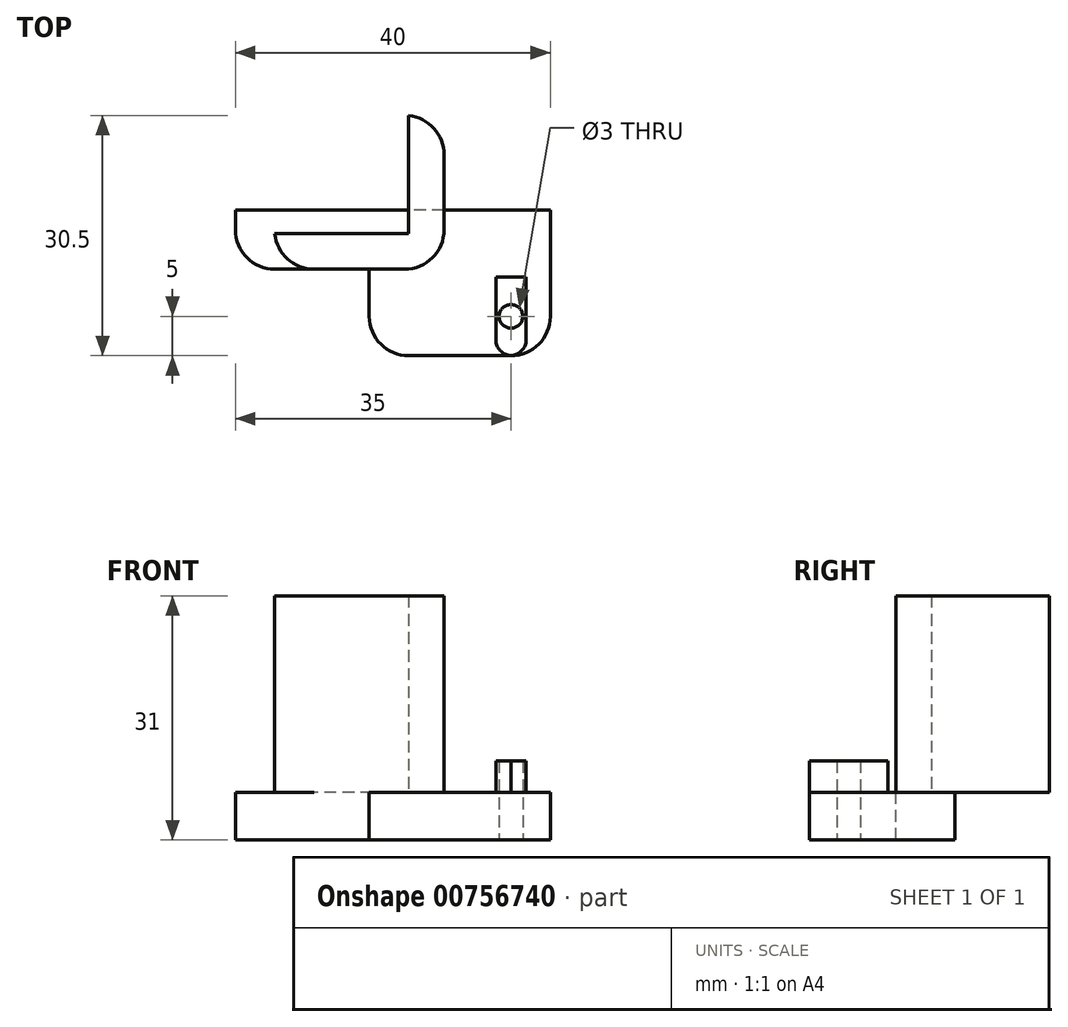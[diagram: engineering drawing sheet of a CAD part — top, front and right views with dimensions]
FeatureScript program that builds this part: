
annotation { "Feature Type Name" : "Feature", "Feature Type Description" : "" }
export const myFeature = defineFeature(function(context is Context, id is Id, definition is map)
    precondition{}
    {
        {
            var Q0;
            Q0=qCreatedBy(makeId("Front.planeOp"),FACE);
            var sketch = newSketch(context, id + "F0", { "sketchPlane" : qUnion([Q0])});
            skLineSegment(sketch, "E0.bottom", {"start": v(11.5, -3) * mm, "end": v(-11.5, -3) * mm});
            skLineSegment(sketch, "E0.top", {"start": v(11.5, 3) * mm, "end": v(-11.5, 3) * mm});
            skLineSegment(sketch, "E0.left", {"start": v(11.5, -3) * mm, "end": v(11.5, 3) * mm});
            skLineSegment(sketch, "E0.right", {"start": v(-11.5, -3) * mm, "end": v(-11.5, 3) * mm});
            skPoint(sketch, "E0.middle", {"position": v(0, 0) * mm});
            skSolve(sketch);
        }
        {
            var Q0;
            Q0=makeQuery(id+"F0.imprint","IMPRINT",FACE,{"disambiguationData":[TD([[makeQuery(id+"F0.imprint","IMPRINT",EDGE,{"derivedFrom":sQuery(id+"F0.wireOp",EDGE,"E0.bottom")}),-1.0]])]});
            extrude(context, id + "F1", {"entities" : qUnion([Q0]), "oppositeDirection" : true, "depth" : 11 * mm, "offsetDistance" : 25 * mm});
        }
        {
            var Q0;
            Q0=makeQuery(id+"F1.opExtrude","SWEPT_FACE",FACE,{"disambiguationData":[OSD([sQuery(id+"F0.wireOp",EDGE,"E0.top")])]});
            var sketch = newSketch(context, id + "F2", { "sketchPlane" : qUnion([Q0])});
            skLineSegment(sketch, "E1", {"start": v(6.5, 0) * mm, "end": v(6.5, 11) * mm, "construction": true});
            skLineSegment(sketch, "E2", {"start": v(-11.5, 5) * mm, "end": v(11.5, 5) * mm, "construction": true});
            skCircle(sketch, "E3", {"center": v(6.5, 5) * mm, "radius": 1.5 * mm});
            skLineSegment(sketch, "E4.bottom", {"start": v(8.42, 9.98) * mm, "end": v(4.58, 9.98) * mm});
            skLineSegment(sketch, "E4.top", {"start": v(8.42, 0.02) * mm, "end": v(4.58, 0.02) * mm});
            skLineSegment(sketch, "E4.left", {"start": v(8.42, 9.98) * mm, "end": v(8.42, 0.02) * mm});
            skLineSegment(sketch, "E4.right", {"start": v(4.58, 9.98) * mm, "end": v(4.58, 0.02) * mm});
            skSolve(sketch);
        }
        {
            var Q0;
            Q0=makeQuery(id+"F2.imprint","IMPRINT",FACE,{"disambiguationData":[TD([[makeQuery(id+"F2.imprint","IMPRINT",EDGE,{"derivedFrom":sQuery(id+"F2.wireOp",EDGE,"E3")}),-1.0]])]});
            extrude(context, id + "F3", {"entities" : qUnion([Q0]), "operationType" : NewBodyOperationType.ADD, "depth" : 4 * mm, "offsetDistance" : 25 * mm});
        }
        {
            var Q0;
            Q0=makeQuery(id+"F3.boolean.opBoolean","SPLIT",FACE,{"disambiguationData":[TD([makeQuery(id+"F3.opExtrude","SWEPT_FACE",FACE,{"disambiguationData":[OSD([sQuery(id+"F2.wireOp",EDGE,"E3")])]})])],"derivedFrom":makeQuery(id+"F1.opExtrude","SWEPT_FACE",FACE,{"disambiguationData":[OSD([sQuery(id+"F0.wireOp",EDGE,"E0.top")])]})});
            extrude(context, id + "F4", {"entities" : qUnion([Q0]), "operationType" : NewBodyOperationType.REMOVE, "oppositeDirection" : true, "depth" : 6 * mm, "offsetDistance" : 25 * mm});
        }
        {
            var Q0;
            Q0=makeQuery(id+"F3.opExtrude","SWEPT_EDGE",EDGE,{"disambiguationData":[OSD([sQuery(id+"F2.wireOp",EDGE,"E4.top"),sQuery(id+"F2.wireOp",EDGE,"E4.left")])]});
            var Q1;
            Q1=makeQuery(id+"F3.opExtrude","SWEPT_EDGE",EDGE,{"disambiguationData":[OSD([sQuery(id+"F2.wireOp",EDGE,"E4.top"),sQuery(id+"F2.wireOp",EDGE,"E4.right")])]});
            fillet(context, id + "F5", {"entities" : qUnion([Q0, Q1]), "radius" : 2 * mm, "tangentPropagation" : true, "allowEdgeOverflow" : false});
        }
        {
            var Q0;
            Q0=makeQuery(id+"F1.opExtrude","CAP_FACE",FACE,{"disambiguationData":[OSD([sQuery(id+"F0.wireOp",EDGE,"E0.bottom"),sQuery(id+"F0.wireOp",EDGE,"E0.top"),sQuery(id+"F0.wireOp",EDGE,"E0.left"),sQuery(id+"F0.wireOp",EDGE,"E0.right")])],"isStart":false});
            var sketch = newSketch(context, id + "F6", { "sketchPlane" : qUnion([Q0])});
            skLineSegment(sketch, "E5.bottom", {"start": v(-11.5, 3) * mm, "end": v(28.5, 3) * mm});
            skLineSegment(sketch, "E5.top", {"start": v(-11.5, -3) * mm, "end": v(28.5, -3) * mm});
            skLineSegment(sketch, "E5.left", {"start": v(-11.5, 3) * mm, "end": v(-11.5, -3) * mm});
            skLineSegment(sketch, "E5.right", {"start": v(28.5, 3) * mm, "end": v(28.5, -3) * mm});
            skSolve(sketch);
        }
        {
            var Q0;
            {var subQ0=sQuery(id+"F6.wireOp",EDGE,"E5.left");Q0=makeQuery(id+"F6.imprint","IMPRINT",FACE,{"disambiguationData":[TD([[makeQuery(id+"F6.imprint","IMPRINT",EDGE,{"derivedFrom":subQ0}),-1.0]])]});}
            var Q1;
            {var subQ2=sQuery(id+"F6.wireOp",EDGE,"E5.right");Q1=makeQuery(id+"F6.imprint","IMPRINT",FACE,{"disambiguationData":[TD([[makeQuery(id+"F6.imprint","IMPRINT",EDGE,{"derivedFrom":subQ2}),-1.0]])]});}
            extrude(context, id + "F7", {"entities" : qUnion([Q0, Q1]), "operationType" : NewBodyOperationType.ADD, "depth" : 4.5 * mm, "offsetDistance" : 25 * mm});
        }
        {
            var Q0;
            {var subQ1=sQuery(id+"F0.wireOp",EDGE,"E0.left");var subQ2=sQuery(id+"F0.wireOp",EDGE,"E0.top");Q0=makeQuery(id+"F7.boolean.opBoolean","MERGE",FACE,{"derivedFrom":[makeQuery(id+"F3.boolean.opBoolean","SPLIT",FACE,{"disambiguationData":[TD([makeQuery(id+"F1.opExtrude","SWEPT_FACE",FACE,{"disambiguationData":[OSD([subQ1])]})])],"derivedFrom":makeQuery(id+"F1.opExtrude","SWEPT_FACE",FACE,{"disambiguationData":[OSD([subQ2])]})}),makeQuery(id+"F7.opExtrude","SWEPT_FACE",FACE,{"disambiguationData":[OSD([sQuery(id+"F6.wireOp",EDGE,"E5.bottom")])]})]});}
            var sketch = newSketch(context, id + "F8", { "sketchPlane" : qUnion([Q0])});
            skLineSegment(sketch, "E6.bottom", {"start": v(-11.5, 11) * mm, "end": v(-23.5, 11) * mm});
            skLineSegment(sketch, "E6.top", {"start": v(-11.5, 15.5) * mm, "end": v(-23.5, 15.5) * mm});
            skLineSegment(sketch, "E6.left", {"start": v(-11.5, 11) * mm, "end": v(-11.5, 15.5) * mm});
            skLineSegment(sketch, "E6.right", {"start": v(-23.5, 11) * mm, "end": v(-23.5, 15.5) * mm});
            skLineSegment(sketch, "E7.bottom", {"start": v(-11.5, 11) * mm, "end": v(-6.5, 11) * mm});
            skLineSegment(sketch, "E7.top", {"start": v(-11.5, 15.5) * mm, "end": v(-6.5, 15.5) * mm});
            skLineSegment(sketch, "E7.right", {"start": v(-6.5, 11) * mm, "end": v(-6.5, 15.5) * mm});
            skSolve(sketch);
        }
        {
            var Q0;
            Q0=makeQuery(id+"F8.imprint","IMPRINT",FACE,{"disambiguationData":[TD([[makeQuery(id+"F8.imprint","IMPRINT",EDGE,{"derivedFrom":sQuery(id+"F8.wireOp",EDGE,"E6.bottom")}),-1.0]])]});
            var Q1;
            Q1=makeQuery(id+"F8.imprint","IMPRINT",FACE,{"disambiguationData":[TD([[makeQuery(id+"F8.imprint","IMPRINT",EDGE,{"derivedFrom":sQuery(id+"F8.wireOp",EDGE,"E7.bottom")}),1.0]])]});
            extrude(context, id + "F9", {"entities" : qUnion([Q0, Q1]), "operationType" : NewBodyOperationType.ADD, "depth" : 25 * mm, "offsetDistance" : 25 * mm});
        }
        {
            var Q0;
            Q0=makeQuery(id+"F9.boolean.opBoolean","MERGE",FACE,{"derivedFrom":[makeQuery(id+"F7.opExtrude","CAP_FACE",FACE,{"disambiguationData":[OSD([sQuery(id+"F6.wireOp",EDGE,"E5.bottom"),sQuery(id+"F6.wireOp",EDGE,"E5.top"),sQuery(id+"F6.wireOp",EDGE,"E5.left"),sQuery(id+"F6.wireOp",EDGE,"E5.right")])],"isStart":false}),makeQuery(id+"F9.opExtrude","SWEPT_FACE",FACE,{"disambiguationData":[OSD([sQuery(id+"F8.wireOp",EDGE,"E6.top"),sQuery(id+"F8.wireOp",EDGE,"E7.top")])]})]});
            var sketch = newSketch(context, id + "F10", { "sketchPlane" : qUnion([Q0])});
            skLineSegment(sketch, "E8.bottom", {"start": v(-11.5, 3) * mm, "end": v(28.5, 3) * mm});
            skLineSegment(sketch, "E8.top", {"start": v(-11.5, -3) * mm, "end": v(28.5, -3) * mm});
            skLineSegment(sketch, "E8.left", {"start": v(-11.5, 3) * mm, "end": v(-11.5, -3) * mm});
            skLineSegment(sketch, "E8.right", {"start": v(28.5, 3) * mm, "end": v(28.5, -3) * mm});
            skSolve(sketch);
        }
        {
            var Q0;
            Q0=makeQuery(id+"F10.imprint","IMPRINT",FACE,{"disambiguationData":[TD([[makeQuery(id+"F10.imprint","IMPRINT",EDGE,{"derivedFrom":sQuery(id+"F10.wireOp",EDGE,"E8.top")}),1.0]])]});
            extrude(context, id + "F11", {"entities" : qUnion([Q0]), "operationType" : NewBodyOperationType.ADD, "depth" : 3 * mm, "offsetDistance" : 25 * mm});
        }
        {
            var Q0;
            Q0=makeQuery(id+"F9.opExtrude","SWEPT_FACE",FACE,{"disambiguationData":[OSD([sQuery(id+"F8.wireOp",EDGE,"E7.right")])]});
            var sketch = newSketch(context, id + "F12", { "sketchPlane" : qUnion([Q0])});
            skLineSegment(sketch, "E9.bottom", {"start": v(11, 28) * mm, "end": v(30.5, 28) * mm});
            skLineSegment(sketch, "E9.top", {"start": v(11, 3) * mm, "end": v(30.5, 3) * mm});
            skLineSegment(sketch, "E9.left", {"start": v(11, 28) * mm, "end": v(11, 3) * mm});
            skLineSegment(sketch, "E9.right", {"start": v(30.5, 28) * mm, "end": v(30.5, 3) * mm});
            skSolve(sketch);
        }
        {
            var Q0;
            {var subQ2=sQuery(id+"F12.wireOp",EDGE,"E9.right");Q0=makeQuery(id+"F12.imprint","IMPRINT",FACE,{"disambiguationData":[TD([[makeQuery(id+"F12.imprint","IMPRINT",EDGE,{"derivedFrom":subQ2}),-1.0]])]});}
            var Q1;
            {var subQ0=sQuery(id+"F12.wireOp",EDGE,"E9.left");Q1=makeQuery(id+"F12.imprint","IMPRINT",FACE,{"disambiguationData":[TD([[makeQuery(id+"F12.imprint","IMPRINT",EDGE,{"derivedFrom":subQ0}),1.0]])]});}
            extrude(context, id + "F13", {"entities" : qUnion([Q0, Q1]), "operationType" : NewBodyOperationType.ADD, "depth" : 4.5 * mm, "offsetDistance" : 25 * mm});
        }
        {
            var Q0;
            Q0=makeQuery(id+"F1.opExtrude","CAP_EDGE",EDGE,{"disambiguationData":[OSD([sQuery(id+"F0.wireOp",EDGE,"E0.right")])],"isStart":false});
            var Q1;
            Q1=makeQuery(id+"F7.opExtrude","CAP_EDGE",EDGE,{"disambiguationData":[OSD([sQuery(id+"F6.wireOp",EDGE,"E5.right")])],"isStart":true});
            var Q2;
            Q2=makeQuery(id+"F1.opExtrude","CAP_EDGE",EDGE,{"disambiguationData":[OSD([sQuery(id+"F0.wireOp",EDGE,"E0.right")])],"isStart":true});
            var Q3;
            Q3=makeQuery(id+"F1.opExtrude","CAP_EDGE",EDGE,{"disambiguationData":[OSD([sQuery(id+"F0.wireOp",EDGE,"E0.left")])],"isStart":true});
            var Q4;
            Q4=makeQuery(id+"F13.opExtrude","CAP_EDGE",EDGE,{"disambiguationData":[OSD([sQuery(id+"F12.wireOp",EDGE,"E9.left")])],"isStart":false});
            var Q5;
            Q5=makeQuery(id+"F9.opExtrude","SWEPT_EDGE",EDGE,{"disambiguationData":[OSD([sQuery(id+"F6.wireOp",EDGE,"E5.bottom"),sQuery(id+"F8.wireOp",EDGE,"E6.bottom"),sQuery(id+"F8.wireOp",EDGE,"E6.right")])]});
            var Q6;
            Q6=makeQuery(id+"F13.opExtrude","CAP_EDGE",EDGE,{"disambiguationData":[OSD([sQuery(id+"F12.wireOp",EDGE,"E9.right")])],"isStart":false});
            fillet(context, id + "F14", {"entities" : qUnion([Q0, Q1, Q2, Q3, Q4, Q5, Q6]), "radius" : 5 * mm, "tangentPropagation" : true, "allowEdgeOverflow" : false});
        }
    });
